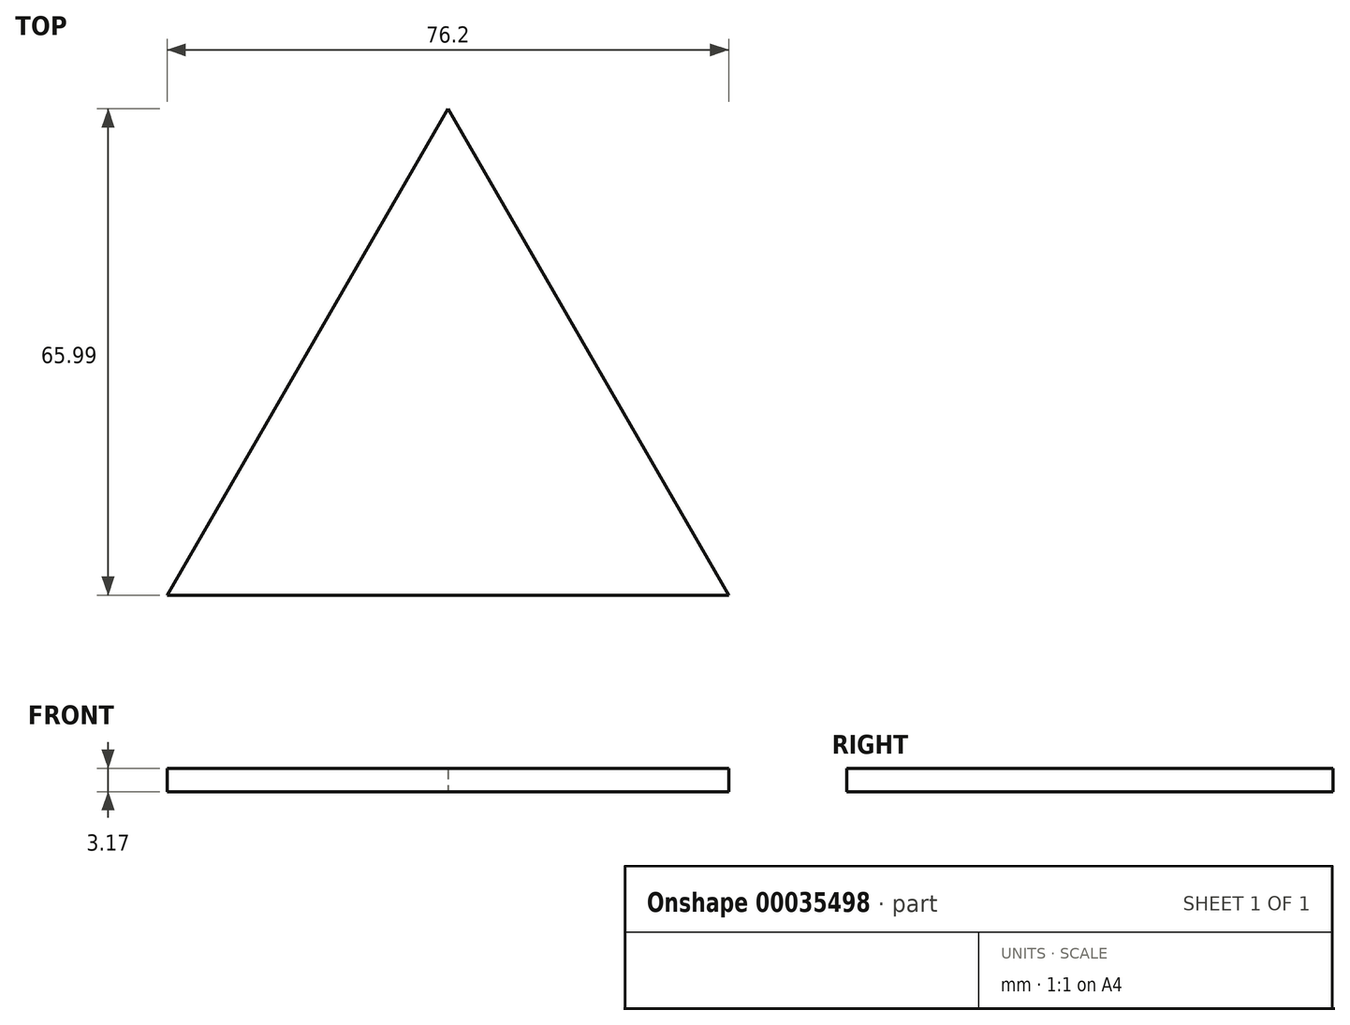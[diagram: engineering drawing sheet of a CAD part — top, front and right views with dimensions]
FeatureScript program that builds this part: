
annotation { "Feature Type Name" : "Feature", "Feature Type Description" : "" }
export const myFeature = defineFeature(function(context is Context, id is Id, definition is map)
    precondition{}
    {
        {
            var Q0;
            Q0=qCreatedBy(makeId("Top.planeOp"),FACE);
            var sketch = newSketch(context, id + "F0", { "sketchPlane" : qUnion([Q0])});
            skLineSegment(sketch, "E0", {"start": v(-38.1, 0) * mm, "end": v(0, 66) * mm});
            skLineSegment(sketch, "E1", {"start": v(0, 66) * mm, "end": v(38.1, 0) * mm});
            skLineSegment(sketch, "E2", {"start": v(38.1, 0) * mm, "end": v(-38.1, 0) * mm});
            skSolve(sketch);
        }
        {
            var Q0;
            Q0=makeQuery(id+"F0.imprint","IMPRINT",FACE,{"disambiguationData":[TD([[makeQuery(id+"F0.imprint","IMPRINT",EDGE,{"derivedFrom":sQuery(id+"F0.wireOp",EDGE,"E0")}),-1.0]])]});
            extrude(context, id + "F1", {"entities" : qUnion([Q0]), "depth" : 3.17 * mm});
        }
    });
